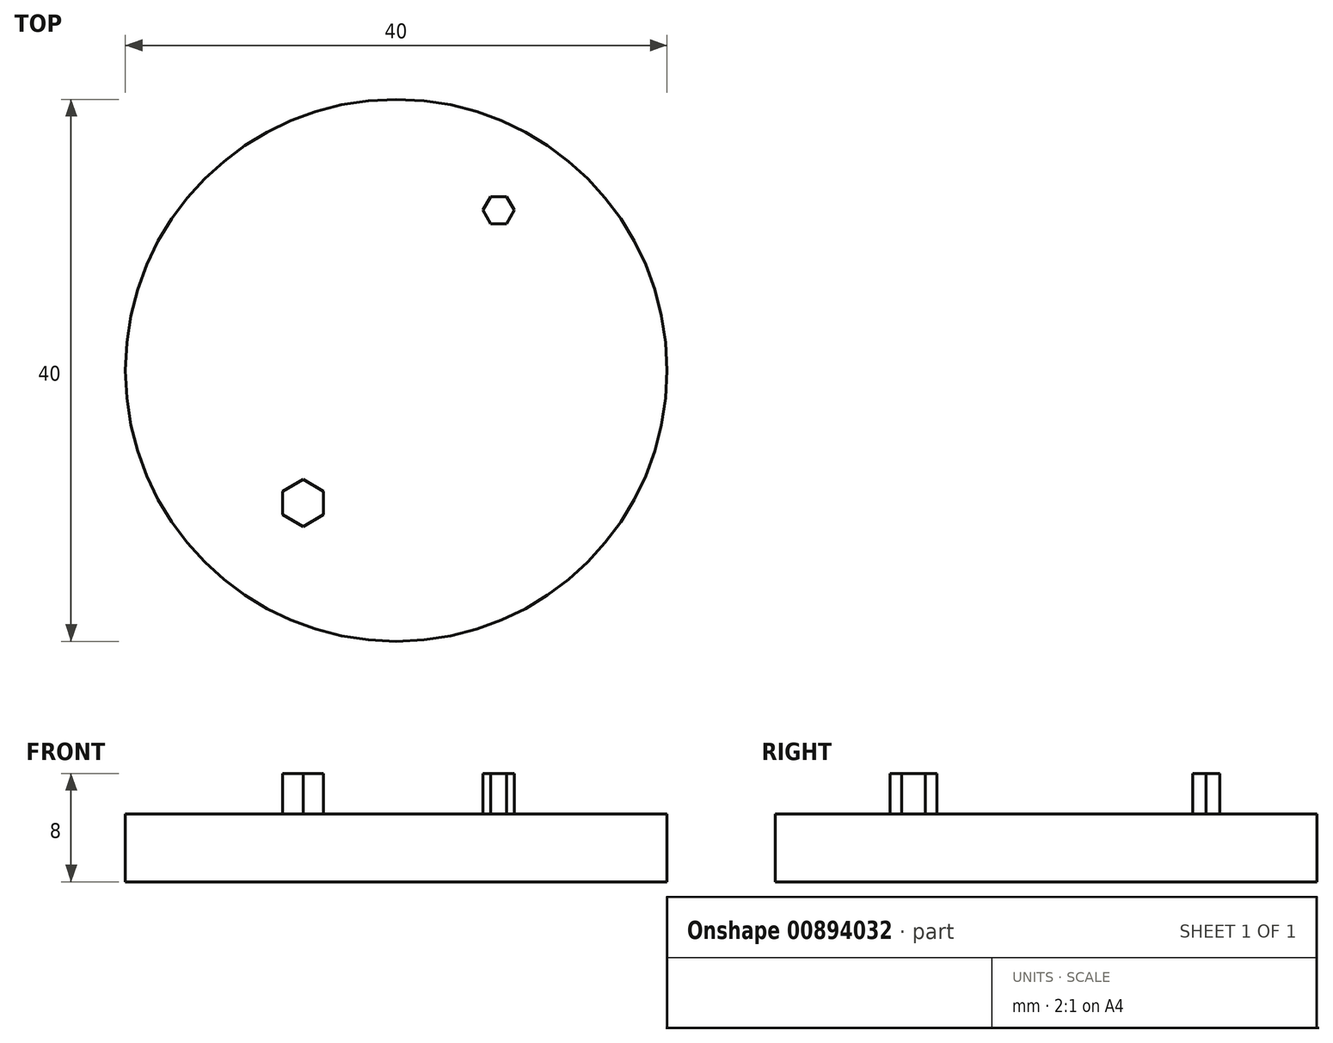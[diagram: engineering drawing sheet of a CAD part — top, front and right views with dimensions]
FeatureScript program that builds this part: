
annotation { "Feature Type Name" : "Feature", "Feature Type Description" : "" }
export const myFeature = defineFeature(function(context is Context, id is Id, definition is map)
    precondition{}
    {
        {
            var Q0;
            Q0=qCreatedBy(makeId("Top.planeOp"),FACE);
            var sketch = newSketch(context, id + "F0", { "sketchPlane" : qUnion([Q0])});
            skCircle(sketch, "E0", {"center": v(0, 0) * mm, "radius": 20 * mm});
            skCircle(sketch, "E1.cCircle", {"center": v(7.57, 11.82) * mm, "radius": 1 * mm, "construction": true});
            skLineSegment(sketch, "E1.0", {"start": v(8.15, 10.82) * mm, "end": v(7, 10.82) * mm});
            skLineSegment(sketch, "E1.1", {"start": v(7, 10.82) * mm, "end": v(6.41, 11.82) * mm});
            skLineSegment(sketch, "E1.2", {"start": v(6.41, 11.82) * mm, "end": v(7, 12.82) * mm});
            skLineSegment(sketch, "E1.3", {"start": v(7, 12.82) * mm, "end": v(8.15, 12.82) * mm});
            skLineSegment(sketch, "E1.4", {"start": v(8.15, 12.82) * mm, "end": v(8.72, 11.82) * mm});
            skLineSegment(sketch, "E1.5", {"start": v(8.72, 11.82) * mm, "end": v(8.15, 10.82) * mm});
            skPoint(sketch, "E1.0.midPoint", {"position": v(7.57, 10.82) * mm});
            skCircle(sketch, "E2.cCircle", {"center": v(-6.88, -9.8) * mm, "radius": 1.5 * mm, "construction": true});
            skLineSegment(sketch, "E2.0", {"start": v(-6.88, -8.06) * mm, "end": v(-5.38, -8.93) * mm});
            skLineSegment(sketch, "E2.1", {"start": v(-5.38, -8.93) * mm, "end": v(-5.38, -10.66) * mm});
            skLineSegment(sketch, "E2.2", {"start": v(-5.38, -10.66) * mm, "end": v(-6.88, -11.52) * mm});
            skLineSegment(sketch, "E2.3", {"start": v(-6.88, -11.52) * mm, "end": v(-8.38, -10.66) * mm});
            skLineSegment(sketch, "E2.4", {"start": v(-8.38, -10.66) * mm, "end": v(-8.38, -8.93) * mm});
            skLineSegment(sketch, "E2.5", {"start": v(-8.38, -8.93) * mm, "end": v(-6.88, -8.06) * mm});
            skPoint(sketch, "E2.0.midPoint", {"position": v(-6.13, -8.5) * mm});
            skSolve(sketch);
        }
        {
            var Q0;
            Q0=makeQuery(id+"F0.imprint","IMPRINT",FACE,{"disambiguationData":[TD([[makeQuery(id+"F0.imprint","IMPRINT",EDGE,{"derivedFrom":sQuery(id+"F0.wireOp",EDGE,"E0")}),1.0]])]});
            var Q1;
            Q1=makeQuery(id+"F0.imprint","IMPRINT",FACE,{"disambiguationData":[TD([[makeQuery(id+"F0.imprint","IMPRINT",EDGE,{"derivedFrom":sQuery(id+"F0.wireOp",EDGE,"E2.0")}),-1.0]])]});
            var Q2;
            Q2=makeQuery(id+"F0.imprint","IMPRINT",FACE,{"disambiguationData":[TD([[makeQuery(id+"F0.imprint","IMPRINT",EDGE,{"derivedFrom":sQuery(id+"F0.wireOp",EDGE,"E1.0")}),-1.0]])]});
            extrude(context, id + "F1", {"entities" : qUnion([Q0, Q1, Q2]), "oppositeDirection" : true, "depth" : 5 * mm, "offsetDistance" : 25 * mm});
        }
        {
            var Q0;
            Q0=makeQuery(id+"F0.imprint","IMPRINT",FACE,{"disambiguationData":[TD([[makeQuery(id+"F0.imprint","IMPRINT",EDGE,{"derivedFrom":sQuery(id+"F0.wireOp",EDGE,"E2.0")}),-1.0]])]});
            var Q1;
            Q1=makeQuery(id+"F0.imprint","IMPRINT",FACE,{"disambiguationData":[TD([[makeQuery(id+"F0.imprint","IMPRINT",EDGE,{"derivedFrom":sQuery(id+"F0.wireOp",EDGE,"E1.0")}),-1.0]])]});
            extrude(context, id + "F2", {"entities" : qUnion([Q0, Q1]), "operationType" : NewBodyOperationType.ADD, "depth" : 3 * mm, "offsetDistance" : 25 * mm});
        }
    });
